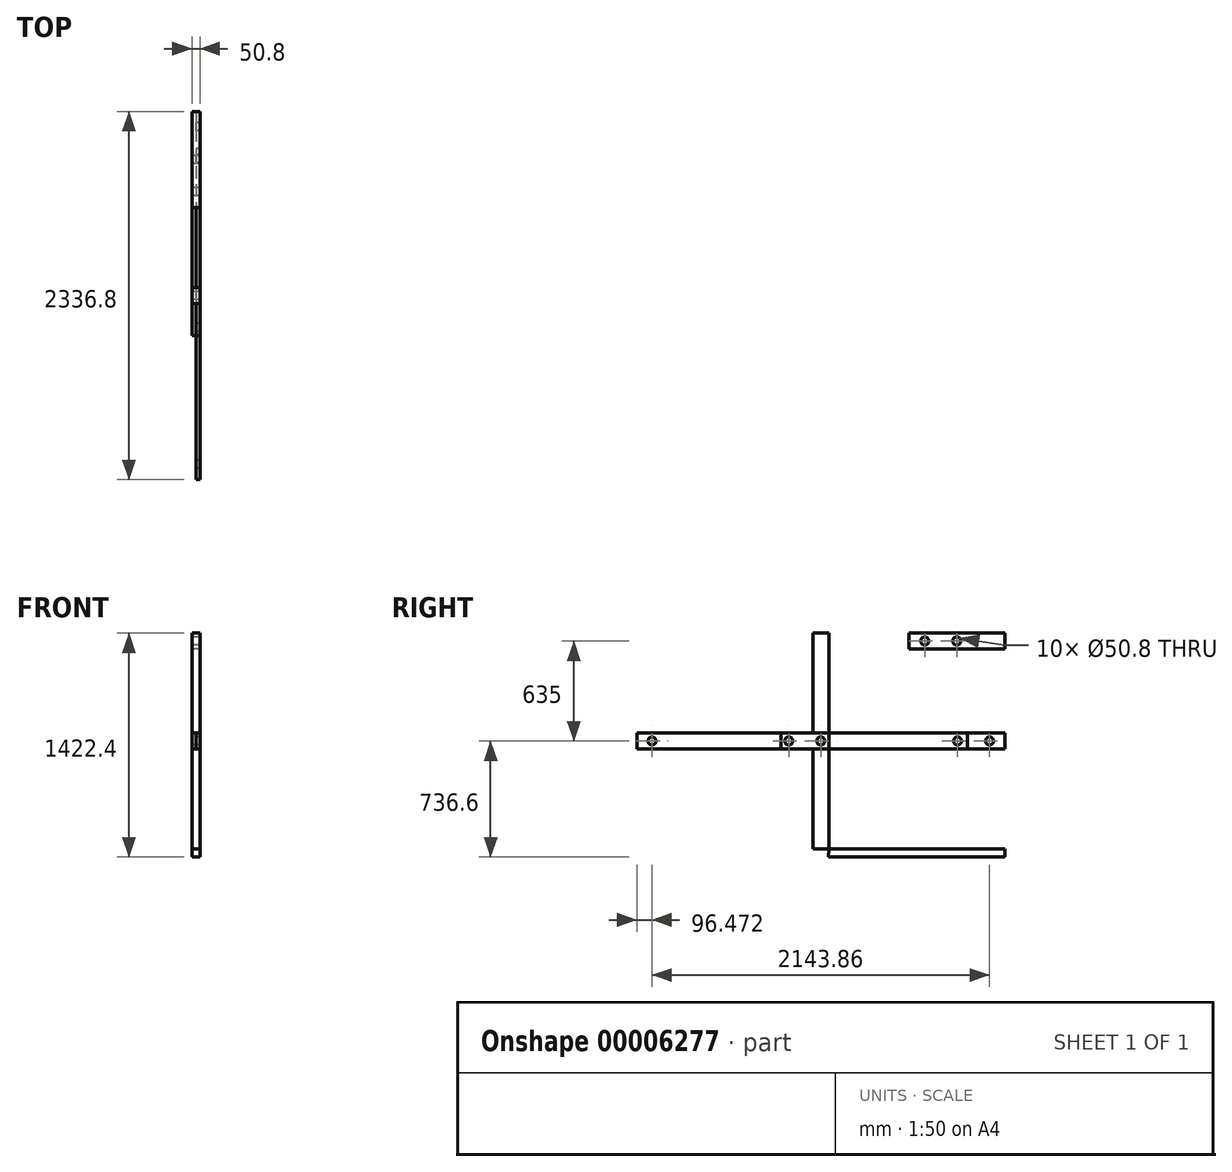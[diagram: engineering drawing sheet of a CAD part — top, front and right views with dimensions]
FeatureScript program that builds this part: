
annotation { "Feature Type Name" : "Feature", "Feature Type Description" : "" }
export const myFeature = defineFeature(function(context is Context, id is Id, definition is map)
    precondition{}
    {
        {
            var Q0;
            Q0=qCreatedBy(makeId("Right.planeOp"),FACE);
            var sketch = newSketch(context, id + "F0", { "sketchPlane" : qUnion([Q0])});
            skLineSegment(sketch, "E0.rect.bottom", {"start": v(-50.8, -685.8) * mm, "end": v(50.8, -685.8) * mm});
            skLineSegment(sketch, "E0.rect.top", {"start": v(-50.8, 685.8) * mm, "end": v(50.8, 685.8) * mm});
            skLineSegment(sketch, "E0.rect.left", {"start": v(-50.8, -685.8) * mm, "end": v(-50.8, 685.8) * mm});
            skLineSegment(sketch, "E0.rect.right", {"start": v(50.8, -685.8) * mm, "end": v(50.8, 685.8) * mm});
            skPoint(sketch, "E0.rect.middle", {"position": v(0, 0) * mm});
            skLineSegment(sketch, "E1.rect.bottom", {"start": v(1168.4, 584.2) * mm, "end": v(558.8, 584.2) * mm});
            skLineSegment(sketch, "E1.rect.top", {"start": v(1168.4, 685.8) * mm, "end": v(558.8, 685.8) * mm});
            skLineSegment(sketch, "E1.rect.left", {"start": v(1168.4, 584.2) * mm, "end": v(1168.4, 685.8) * mm});
            skLineSegment(sketch, "E1.rect.right", {"start": v(558.8, 584.2) * mm, "end": v(558.8, 685.8) * mm});
            skPoint(sketch, "E1.rect.middle", {"position": v(863.6, 635) * mm});
            skLineSegment(sketch, "E2", {"start": v(-50.8, 685.8) * mm, "end": v(863.6, 685.8) * mm, "construction": true});
            skLineSegment(sketch, "E3", {"start": v(558.8, 635) * mm, "end": v(1168.4, 635) * mm, "construction": true});
            skPoint(sketch, "E4", {"position": v(660.4, 635) * mm});
            skCircle(sketch, "E5", {"center": v(0, 0) * mm, "radius": 1071.93 * mm, "construction": true});
            skLineSegment(sketch, "E6", {"start": v(50.8, -685.8) * mm, "end": v(1168.4, -685.8) * mm});
            skLineSegment(sketch, "E7", {"start": v(1168.4, -685.8) * mm, "end": v(1168.4, -736.6) * mm});
            skLineSegment(sketch, "E8", {"start": v(1168.4, -736.6) * mm, "end": v(50.46, -736.6) * mm});
            skLineSegment(sketch, "E9", {"start": v(50.46, -736.6) * mm, "end": v(50.8, -685.8) * mm});
            skLineSegment(sketch, "E10.rect.bottom", {"start": v(1168.4, -50.8) * mm, "end": v(-1168.4, -50.8) * mm});
            skLineSegment(sketch, "E10.rect.top", {"start": v(1168.4, 50.8) * mm, "end": v(-1168.4, 50.8) * mm});
            skLineSegment(sketch, "E10.rect.left", {"start": v(1168.4, -50.8) * mm, "end": v(1168.4, 50.8) * mm});
            skLineSegment(sketch, "E10.rect.right", {"start": v(-1168.4, -50.8) * mm, "end": v(-1168.4, 50.8) * mm});
            skLineSegment(sketch, "E11.rect.bottom", {"start": v(254, -50.8) * mm, "end": v(-254, -50.8) * mm});
            skLineSegment(sketch, "E11.rect.top", {"start": v(254, 50.8) * mm, "end": v(-254, 50.8) * mm});
            skLineSegment(sketch, "E11.rect.left", {"start": v(254, -50.8) * mm, "end": v(254, 50.8) * mm});
            skLineSegment(sketch, "E11.rect.right", {"start": v(-254, -50.8) * mm, "end": v(-254, 50.8) * mm});
            skCircle(sketch, "E12", {"center": v(-1071.93, 0) * mm, "radius": 25.4 * mm});
            skCircle(sketch, "E13", {"center": v(-203.2, 0) * mm, "radius": 25.4 * mm});
            skCircle(sketch, "E14", {"center": v(868.73, 0) * mm, "radius": 25.4 * mm});
            skCircle(sketch, "E15", {"center": v(1071.93, 0) * mm, "radius": 25.4 * mm});
            skCircle(sketch, "E16", {"center": v(660.4, 635) * mm, "radius": 25.4 * mm});
            skCircle(sketch, "E17", {"center": v(863.6, 635) * mm, "radius": 25.4 * mm});
            skCircle(sketch, "E18", {"center": v(0, 0) * mm, "radius": 25.4 * mm});
            skLineSegment(sketch, "E19", {"start": v(1026.8, 307.74) * mm, "end": v(823.6, 307.74) * mm, "construction": true});
            skLineSegment(sketch, "E20", {"start": v(954.31, 488.17) * mm, "end": v(751.11, 488.17) * mm, "construction": true});
            skLineSegment(sketch, "E21", {"start": v(1060.33, -157.25) * mm, "end": v(857.13, -157.25) * mm, "construction": true});
            skLineSegment(sketch, "E22", {"start": v(1009.65, -360.04) * mm, "end": v(806.45, -360.04) * mm, "construction": true});
            skLineSegment(sketch, "E23", {"start": v(932.68, -528.33) * mm, "end": v(729.48, -528.33) * mm, "construction": true});
            skCircle(sketch, "E24", {"center": v(-203.2, 0) * mm, "radius": 1071.93 * mm, "construction": true});
            skLineSegment(sketch, "E25.bottom", {"start": v(-1117.6, 38.1) * mm, "end": v(-165.1, 38.1) * mm});
            skLineSegment(sketch, "E25.top", {"start": v(-1117.6, -38.1) * mm, "end": v(-165.1, -38.1) * mm});
            skLineSegment(sketch, "E25.left", {"start": v(-1117.6, 38.1) * mm, "end": v(-1117.6, -38.1) * mm});
            skLineSegment(sketch, "E25.right", {"start": v(-165.1, 38.1) * mm, "end": v(-165.1, -38.1) * mm});
            skLineSegment(sketch, "E26", {"start": v(-1117.6, 0) * mm, "end": v(-165.1, 0) * mm, "construction": true});
            skLineSegment(sketch, "E27", {"start": v(932.18, 50.8) * mm, "end": v(932.18, -50.8) * mm});
            skSolve(sketch);
        }
        {
            var Q0;
            {var subQ5=sQuery(id+"F0.wireOp",EDGE,"E0.rect.top");Q0=makeQuery(id+"F0.imprint","IMPRINT",FACE,{"disambiguationData":[TD([[makeQuery(id+"F0.imprint","IMPRINT",EDGE,{"derivedFrom":subQ5}),-1.0]])]});}
            var Q1;
            {var subQ3=sQuery(id+"F0.wireOp",EDGE,"E0.rect.left");var subQ5=sQuery(id+"F0.wireOp",EDGE,"E10.rect.top");var subQ7=makeQuery(id+"F0.imprint","INTERSECT",VERTEX,{"derivedFrom":[subQ3,subQ5]});Q1=makeQuery(id+"F0.imprint","IMPRINT",FACE,{"disambiguationData":[TD([[makeQuery(id+"F0.imprint","IMPRINT",EDGE,{"disambiguationData":[TD([[subQ7,1.0]])],"derivedFrom":subQ3}),-1.0]])]});}
            var Q2;
            {var subQ3=sQuery(id+"F0.wireOp",EDGE,"E0.rect.left");var subQ5=sQuery(id+"F0.wireOp",EDGE,"E11.rect.bottom");var subQ7=makeQuery(id+"F0.imprint","INTERSECT",VERTEX,{"derivedFrom":[subQ3,subQ5]});Q2=makeQuery(id+"F0.imprint","IMPRINT",FACE,{"disambiguationData":[TD([[makeQuery(id+"F0.imprint","IMPRINT",EDGE,{"disambiguationData":[TD([[subQ7,-1.0]])],"derivedFrom":subQ3}),-1.0]])]});}
            var Q3;
            {var subQ3=sQuery(id+"F0.wireOp",EDGE,"E0.rect.left");var subQ5=sQuery(id+"F0.wireOp",EDGE,"E10.rect.bottom");var subQ7=makeQuery(id+"F0.imprint","INTERSECT",VERTEX,{"derivedFrom":[subQ3,subQ5]});Q3=makeQuery(id+"F0.imprint","IMPRINT",FACE,{"disambiguationData":[TD([[makeQuery(id+"F0.imprint","IMPRINT",EDGE,{"disambiguationData":[TD([[subQ7,-1.0]])],"derivedFrom":subQ3}),-1.0]])]});}
            var Q4;
            {var subQ5=sQuery(id+"F0.wireOp",EDGE,"E0.rect.bottom");Q4=makeQuery(id+"F0.imprint","IMPRINT",FACE,{"disambiguationData":[TD([[makeQuery(id+"F0.imprint","IMPRINT",EDGE,{"derivedFrom":subQ5}),1.0]])]});}
            var Q5;
            Q5=makeQuery(id+"F0.imprint","IMPRINT",FACE,{"disambiguationData":[TD([[makeQuery(id+"F0.imprint","IMPRINT",EDGE,{"derivedFrom":sQuery(id+"F0.wireOp",EDGE,"E6")}),-1.0]])]});
            var Q6;
            Q6=makeQuery(id+"F0.imprint","IMPRINT",FACE,{"disambiguationData":[TD([[makeQuery(id+"F0.imprint","IMPRINT",EDGE,{"derivedFrom":sQuery(id+"F0.wireOp",EDGE,"E1.rect.bottom")}),-1.0]])]});
            var Q7;
            {var subQ0=sQuery(id+"F0.wireOp",EDGE,"E25.right");Q7=makeQuery(id+"F0.imprint","IMPRINT",FACE,{"disambiguationData":[TD([[makeQuery(id+"F0.imprint","IMPRINT",EDGE,{"derivedFrom":subQ0}),1.0]])]});}
            var Q8;
            Q8=makeQuery(id+"F0.imprint","IMPRINT",FACE,{"disambiguationData":[TD([[makeQuery(id+"F0.imprint","IMPRINT",EDGE,{"derivedFrom":sQuery(id+"F0.wireOp",EDGE,"E13")}),-1.0]])]});
            extrude(context, id + "F1", {"entities" : qUnion([Q0, Q1, Q2, Q3, Q4, Q5, Q6, Q7, Q8]), "endBound" : BoundingType.SYMMETRIC, "depth" : 50.8 * mm});
        }
        {
            var Q0;
            {var subQ1=sQuery(id+"F0.wireOp",EDGE,"E10.rect.left");Q0=makeQuery(id+"F0.imprint","IMPRINT",FACE,{"disambiguationData":[TD([[makeQuery(id+"F0.imprint","IMPRINT",EDGE,{"derivedFrom":subQ1}),1.0]])]});}
            var Q1;
            Q1=makeQuery(id+"F0.imprint","IMPRINT",FACE,{"disambiguationData":[TD([[makeQuery(id+"F0.imprint","IMPRINT",EDGE,{"derivedFrom":sQuery(id+"F0.wireOp",EDGE,"E14")}),1.0]])]});
            var Q2;
            {var subQ0=sQuery(id+"F0.wireOp",EDGE,"E11.rect.left");Q2=makeQuery(id+"F0.imprint","IMPRINT",FACE,{"disambiguationData":[TD([[makeQuery(id+"F0.imprint","IMPRINT",EDGE,{"derivedFrom":subQ0}),1.0]])]});}
            var Q3;
            Q3=makeQuery(id+"F0.imprint","IMPRINT",FACE,{"disambiguationData":[TD([[makeQuery(id+"F0.imprint","IMPRINT",EDGE,{"derivedFrom":sQuery(id+"F0.wireOp",EDGE,"E18")}),-1.0]])]});
            var Q4;
            {var subQ0=sQuery(id+"F0.wireOp",EDGE,"E25.right");Q4=makeQuery(id+"F0.imprint","IMPRINT",FACE,{"disambiguationData":[TD([[makeQuery(id+"F0.imprint","IMPRINT",EDGE,{"derivedFrom":subQ0}),1.0]])]});}
            var Q5;
            Q5=makeQuery(id+"F0.imprint","IMPRINT",FACE,{"disambiguationData":[TD([[makeQuery(id+"F0.imprint","IMPRINT",EDGE,{"derivedFrom":sQuery(id+"F0.wireOp",EDGE,"E13")}),1.0]])]});
            var Q6;
            Q6=makeQuery(id+"F0.imprint","IMPRINT",FACE,{"disambiguationData":[TD([[makeQuery(id+"F0.imprint","IMPRINT",EDGE,{"derivedFrom":sQuery(id+"F0.wireOp",EDGE,"E13")}),-1.0]])]});
            var Q7;
            Q7=makeQuery(id+"F0.imprint","IMPRINT",FACE,{"disambiguationData":[TD([[makeQuery(id+"F0.imprint","IMPRINT",EDGE,{"derivedFrom":sQuery(id+"F0.wireOp",EDGE,"E12")}),-1.0]])]});
            var Q8;
            {var subQ10=sQuery(id+"F0.wireOp",EDGE,"E10.rect.right");Q8=makeQuery(id+"F0.imprint","IMPRINT",FACE,{"disambiguationData":[TD([[makeQuery(id+"F0.imprint","IMPRINT",EDGE,{"derivedFrom":subQ10}),-1.0]])]});}
            var Q9;
            {var subQ1=sQuery(id+"F0.wireOp",EDGE,"E11.rect.left");Q9=makeQuery(id+"F0.imprint","IMPRINT",FACE,{"disambiguationData":[TD([[makeQuery(id+"F0.imprint","IMPRINT",EDGE,{"derivedFrom":subQ1}),-1.0]])]});}
            extrude(context, id + "F2", {"entities" : qUnion([Q0, Q1, Q2, Q3, Q4, Q5, Q6, Q7, Q8, Q9]), "depth" : 25.4 * mm});
        }
        {
            var Q0;
            {var subQ1=sQuery(id+"F0.wireOp",EDGE,"E11.rect.left");Q0=makeQuery(id+"F0.imprint","IMPRINT",FACE,{"disambiguationData":[TD([[makeQuery(id+"F0.imprint","IMPRINT",EDGE,{"derivedFrom":subQ1}),-1.0]])]});}
            var Q1;
            {var subQ0=sQuery(id+"F0.wireOp",EDGE,"E11.rect.left");Q1=makeQuery(id+"F0.imprint","IMPRINT",FACE,{"disambiguationData":[TD([[makeQuery(id+"F0.imprint","IMPRINT",EDGE,{"derivedFrom":subQ0}),1.0]])]});}
            var Q2;
            Q2=makeQuery(id+"F0.imprint","IMPRINT",FACE,{"disambiguationData":[TD([[makeQuery(id+"F0.imprint","IMPRINT",EDGE,{"derivedFrom":sQuery(id+"F0.wireOp",EDGE,"E18")}),-1.0]])]});
            var Q3;
            {var subQ0=sQuery(id+"F0.wireOp",EDGE,"E25.right");Q3=makeQuery(id+"F0.imprint","IMPRINT",FACE,{"disambiguationData":[TD([[makeQuery(id+"F0.imprint","IMPRINT",EDGE,{"derivedFrom":subQ0}),1.0]])]});}
            var Q4;
            Q4=makeQuery(id+"F0.imprint","IMPRINT",FACE,{"disambiguationData":[TD([[makeQuery(id+"F0.imprint","IMPRINT",EDGE,{"derivedFrom":sQuery(id+"F0.wireOp",EDGE,"E13")}),-1.0]])]});
            extrude(context, id + "F3", {"entities" : qUnion([Q0, Q1, Q2, Q3, Q4]), "depth" : 25.4 * mm});
        }
    });
